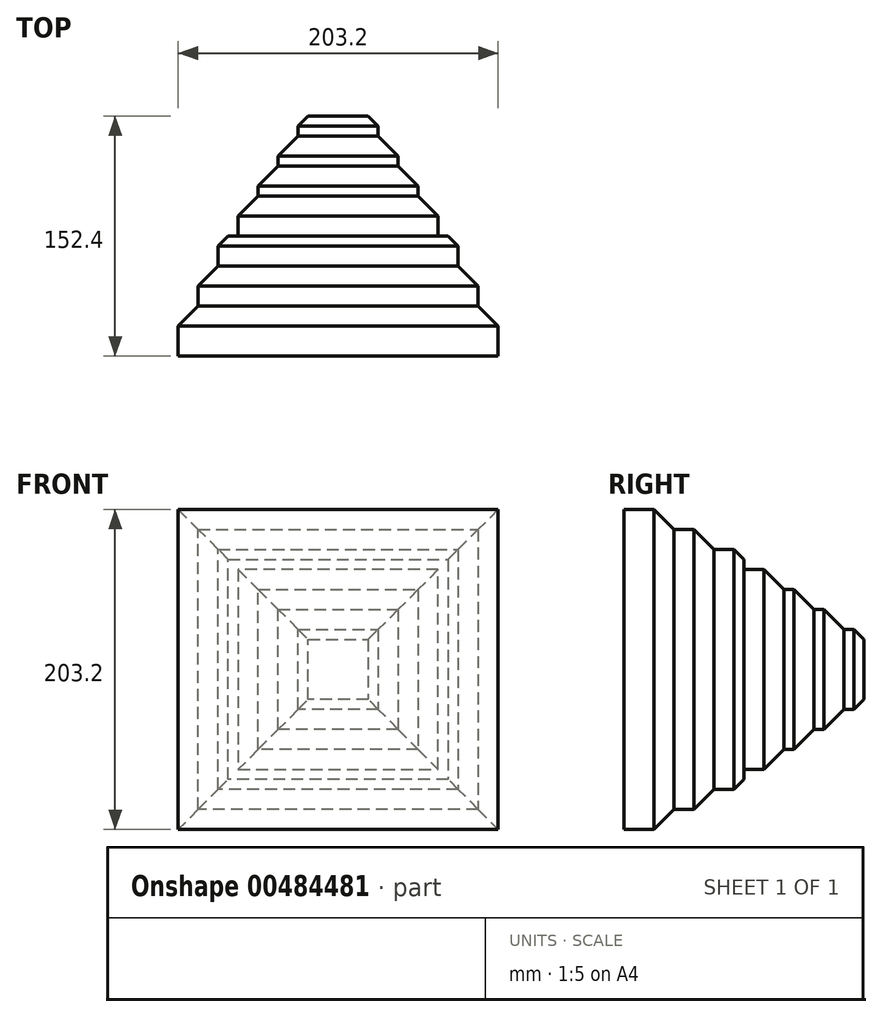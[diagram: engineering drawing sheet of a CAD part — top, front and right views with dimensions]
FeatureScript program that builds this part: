
annotation { "Feature Type Name" : "Feature", "Feature Type Description" : "" }
export const myFeature = defineFeature(function(context is Context, id is Id, definition is map)
    precondition{}
    {
        {
            var Q0;
            Q0=qCreatedBy(makeId("Front.planeOp"),FACE);
            var sketch = newSketch(context, id + "F0", { "sketchPlane" : qUnion([Q0])});
            skLineSegment(sketch, "E0.bottom", {"start": v(0, 0) * mm, "end": v(101.6, 0) * mm});
            skLineSegment(sketch, "E0.top", {"start": v(0, 101.6) * mm, "end": v(101.6, 101.6) * mm});
            skLineSegment(sketch, "E0.left", {"start": v(0, 0) * mm, "end": v(0, 101.6) * mm});
            skLineSegment(sketch, "E0.right", {"start": v(101.6, 0) * mm, "end": v(101.6, 101.6) * mm});
            skLineSegment(sketch, "E1.top", {"start": v(0, -101.6) * mm, "end": v(101.6, -101.6) * mm});
            skLineSegment(sketch, "E1.left", {"start": v(0, 0) * mm, "end": v(0, -101.6) * mm});
            skLineSegment(sketch, "E1.right", {"start": v(101.6, 0) * mm, "end": v(101.6, -101.6) * mm});
            skLineSegment(sketch, "E2.bottom", {"start": v(0, 0) * mm, "end": v(-101.6, 0) * mm});
            skLineSegment(sketch, "E2.top", {"start": v(0, -101.6) * mm, "end": v(-101.6, -101.6) * mm});
            skLineSegment(sketch, "E2.right", {"start": v(-101.6, 0) * mm, "end": v(-101.6, -101.6) * mm});
            skLineSegment(sketch, "E3.top", {"start": v(0, 101.6) * mm, "end": v(-101.6, 101.6) * mm});
            skLineSegment(sketch, "E3.right", {"start": v(-101.6, 0) * mm, "end": v(-101.6, 101.6) * mm});
            skSolve(sketch);
        }
        {
            var Q0;
            Q0=makeQuery(id+"F0.imprint","IMPRINT",FACE,{"disambiguationData":[TD([[makeQuery(id+"F0.imprint","IMPRINT",EDGE,{"derivedFrom":sQuery(id+"F0.wireOp",EDGE,"E2.bottom")}),-1.0]])]});
            var Q1;
            Q1=makeQuery(id+"F0.imprint","IMPRINT",FACE,{"disambiguationData":[TD([[makeQuery(id+"F0.imprint","IMPRINT",EDGE,{"derivedFrom":sQuery(id+"F0.wireOp",EDGE,"E0.top")}),-1.0]])]});
            var Q2;
            Q2=makeQuery(id+"F0.imprint","IMPRINT",FACE,{"disambiguationData":[TD([[makeQuery(id+"F0.imprint","IMPRINT",EDGE,{"derivedFrom":sQuery(id+"F0.wireOp",EDGE,"E0.bottom")}),-1.0]])]});
            var Q3;
            Q3=makeQuery(id+"F0.imprint","IMPRINT",FACE,{"disambiguationData":[TD([[makeQuery(id+"F0.imprint","IMPRINT",EDGE,{"derivedFrom":sQuery(id+"F0.wireOp",EDGE,"E2.top")}),-1.0]])]});
            extrude(context, id + "F1", {"entities" : qUnion([Q0, Q1, Q2, Q3]), "oppositeDirection" : true, "depth" : 25.4 * mm});
        }
        {
            var Q0;
            Q0=makeQuery(id+"F1.opExtrude","CAP_FACE",FACE,{"disambiguationData":[OSD([sQuery(id+"F0.wireOp",EDGE,"E0.top"),sQuery(id+"F0.wireOp",EDGE,"E0.right"),sQuery(id+"F0.wireOp",EDGE,"E1.top"),sQuery(id+"F0.wireOp",EDGE,"E1.right"),sQuery(id+"F0.wireOp",EDGE,"E2.top"),sQuery(id+"F0.wireOp",EDGE,"E2.right"),sQuery(id+"F0.wireOp",EDGE,"E3.top"),sQuery(id+"F0.wireOp",EDGE,"E3.right")])],"isStart":false});
            var sketch = newSketch(context, id + "F2", { "sketchPlane" : qUnion([Q0])});
            skLineSegment(sketch, "E4.bottom", {"start": v(0, 0) * mm, "end": v(88.9, 0) * mm});
            skLineSegment(sketch, "E4.top", {"start": v(0, 88.9) * mm, "end": v(88.9, 88.9) * mm});
            skLineSegment(sketch, "E4.left", {"start": v(0, 0) * mm, "end": v(0, 88.9) * mm});
            skLineSegment(sketch, "E4.right", {"start": v(88.9, 0) * mm, "end": v(88.9, 88.9) * mm});
            skLineSegment(sketch, "E5.top", {"start": v(0, -88.9) * mm, "end": v(88.9, -88.9) * mm});
            skLineSegment(sketch, "E5.left", {"start": v(0, 0) * mm, "end": v(0, -88.9) * mm});
            skLineSegment(sketch, "E5.right", {"start": v(88.9, 0) * mm, "end": v(88.9, -88.9) * mm});
            skLineSegment(sketch, "E6.bottom", {"start": v(0, 0) * mm, "end": v(-88.9, 0) * mm});
            skLineSegment(sketch, "E6.top", {"start": v(0, -88.9) * mm, "end": v(-88.9, -88.9) * mm});
            skLineSegment(sketch, "E6.right", {"start": v(-88.9, 0) * mm, "end": v(-88.9, -88.9) * mm});
            skLineSegment(sketch, "E7.top", {"start": v(0, 88.9) * mm, "end": v(-88.9, 88.9) * mm});
            skLineSegment(sketch, "E7.right", {"start": v(-88.9, 0) * mm, "end": v(-88.9, 88.9) * mm});
            skSolve(sketch);
        }
        {
            var Q0;
            Q0=makeQuery(id+"F2.imprint","IMPRINT",FACE,{"disambiguationData":[TD([[makeQuery(id+"F2.imprint","IMPRINT",EDGE,{"derivedFrom":sQuery(id+"F2.wireOp",EDGE,"E6.bottom")}),-1.0]])]});
            var Q1;
            Q1=makeQuery(id+"F2.imprint","IMPRINT",FACE,{"disambiguationData":[TD([[makeQuery(id+"F2.imprint","IMPRINT",EDGE,{"derivedFrom":sQuery(id+"F2.wireOp",EDGE,"E4.top")}),-1.0]])]});
            var Q2;
            Q2=makeQuery(id+"F2.imprint","IMPRINT",FACE,{"disambiguationData":[TD([[makeQuery(id+"F2.imprint","IMPRINT",EDGE,{"derivedFrom":sQuery(id+"F2.wireOp",EDGE,"E4.bottom")}),-1.0]])]});
            var Q3;
            Q3=makeQuery(id+"F2.imprint","IMPRINT",FACE,{"disambiguationData":[TD([[makeQuery(id+"F2.imprint","IMPRINT",EDGE,{"derivedFrom":sQuery(id+"F2.wireOp",EDGE,"E6.top")}),-1.0]])]});
            extrude(context, id + "F3", {"entities" : qUnion([Q0, Q1, Q2, Q3]), "operationType" : NewBodyOperationType.ADD, "depth" : 25.4 * mm});
        }
        {
            var Q0;
            Q0=makeQuery(id+"F3.opExtrude","CAP_FACE",FACE,{"disambiguationData":[OSD([sQuery(id+"F2.wireOp",EDGE,"E4.top"),sQuery(id+"F2.wireOp",EDGE,"E4.right"),sQuery(id+"F2.wireOp",EDGE,"E5.top"),sQuery(id+"F2.wireOp",EDGE,"E5.right"),sQuery(id+"F2.wireOp",EDGE,"E6.top"),sQuery(id+"F2.wireOp",EDGE,"E6.right"),sQuery(id+"F2.wireOp",EDGE,"E7.top"),sQuery(id+"F2.wireOp",EDGE,"E7.right")])],"isStart":false});
            var sketch = newSketch(context, id + "F4", { "sketchPlane" : qUnion([Q0])});
            skLineSegment(sketch, "E8.bottom", {"start": v(0, 0) * mm, "end": v(-76.2, 0) * mm});
            skLineSegment(sketch, "E8.top", {"start": v(0, -76.2) * mm, "end": v(-76.2, -76.2) * mm});
            skLineSegment(sketch, "E8.left", {"start": v(0, 0) * mm, "end": v(0, -76.2) * mm});
            skLineSegment(sketch, "E8.right", {"start": v(-76.2, 0) * mm, "end": v(-76.2, -76.2) * mm});
            skLineSegment(sketch, "E9.bottom", {"start": v(0, 0) * mm, "end": v(76.2, 0) * mm});
            skLineSegment(sketch, "E9.top", {"start": v(0, -76.2) * mm, "end": v(76.2, -76.2) * mm});
            skLineSegment(sketch, "E9.right", {"start": v(76.2, 0) * mm, "end": v(76.2, -76.2) * mm});
            skLineSegment(sketch, "E10.top", {"start": v(0, 76.2) * mm, "end": v(76.2, 76.2) * mm});
            skLineSegment(sketch, "E10.left", {"start": v(0, 0) * mm, "end": v(0, 76.2) * mm});
            skLineSegment(sketch, "E10.right", {"start": v(76.2, 0) * mm, "end": v(76.2, 76.2) * mm});
            skLineSegment(sketch, "E11.top", {"start": v(0, 76.2) * mm, "end": v(-76.2, 76.2) * mm});
            skLineSegment(sketch, "E11.right", {"start": v(-76.2, 0) * mm, "end": v(-76.2, 76.2) * mm});
            skSolve(sketch);
        }
        {
            var Q0;
            Q0=makeQuery(id+"F4.imprint","IMPRINT",FACE,{"disambiguationData":[TD([[makeQuery(id+"F4.imprint","IMPRINT",EDGE,{"derivedFrom":sQuery(id+"F4.wireOp",EDGE,"E8.bottom")}),-1.0]])]});
            var Q1;
            Q1=makeQuery(id+"F4.imprint","IMPRINT",FACE,{"disambiguationData":[TD([[makeQuery(id+"F4.imprint","IMPRINT",EDGE,{"derivedFrom":sQuery(id+"F4.wireOp",EDGE,"E9.bottom")}),1.0]])]});
            var Q2;
            Q2=makeQuery(id+"F4.imprint","IMPRINT",FACE,{"disambiguationData":[TD([[makeQuery(id+"F4.imprint","IMPRINT",EDGE,{"derivedFrom":sQuery(id+"F4.wireOp",EDGE,"E9.top")}),1.0]])]});
            var Q3;
            Q3=makeQuery(id+"F4.imprint","IMPRINT",FACE,{"disambiguationData":[TD([[makeQuery(id+"F4.imprint","IMPRINT",EDGE,{"derivedFrom":sQuery(id+"F4.wireOp",EDGE,"E8.top")}),-1.0]])]});
            var Q4;
            Q4 = qSketchRegion(id + "F6", true);
            extrude(context, id + "F5", {"entities" : qUnion([Q0, Q1, Q2, Q3, Q4]), "operationType" : NewBodyOperationType.ADD, "depth" : 25.4 * mm});
        }
        {
            var Q0;
            Q0=makeQuery(id+"F5.opExtrude","CAP_FACE",FACE,{"disambiguationData":[OSD([sQuery(id+"F4.wireOp",EDGE,"E8.top"),sQuery(id+"F4.wireOp",EDGE,"E8.right"),sQuery(id+"F4.wireOp",EDGE,"E9.top"),sQuery(id+"F4.wireOp",EDGE,"E9.right"),sQuery(id+"F4.wireOp",EDGE,"E10.top"),sQuery(id+"F4.wireOp",EDGE,"E10.right"),sQuery(id+"F4.wireOp",EDGE,"E11.top"),sQuery(id+"F4.wireOp",EDGE,"E11.right")])],"isStart":false});
            var sketch = newSketch(context, id + "F6", { "sketchPlane" : qUnion([Q0])});
            skLineSegment(sketch, "E12.bottom", {"start": v(0, 0) * mm, "end": v(-63.5, 0) * mm});
            skLineSegment(sketch, "E12.top", {"start": v(0, -63.5) * mm, "end": v(-63.5, -63.5) * mm});
            skLineSegment(sketch, "E12.left", {"start": v(0, 0) * mm, "end": v(0, -63.5) * mm});
            skLineSegment(sketch, "E12.right", {"start": v(-63.5, 0) * mm, "end": v(-63.5, -63.5) * mm});
            skLineSegment(sketch, "E13.bottom", {"start": v(0, 0) * mm, "end": v(63.5, 0) * mm});
            skLineSegment(sketch, "E13.top", {"start": v(0, -63.5) * mm, "end": v(63.5, -63.5) * mm});
            skLineSegment(sketch, "E13.right", {"start": v(63.5, 0) * mm, "end": v(63.5, -63.5) * mm});
            skLineSegment(sketch, "E14.top", {"start": v(0, 63.5) * mm, "end": v(63.5, 63.5) * mm});
            skLineSegment(sketch, "E14.left", {"start": v(0, 0) * mm, "end": v(0, 63.5) * mm});
            skLineSegment(sketch, "E14.right", {"start": v(63.5, 0) * mm, "end": v(63.5, 63.5) * mm});
            skLineSegment(sketch, "E15.top", {"start": v(0, 63.5) * mm, "end": v(-63.5, 63.5) * mm});
            skLineSegment(sketch, "E15.right", {"start": v(-63.5, 0) * mm, "end": v(-63.5, 63.5) * mm});
            skSolve(sketch);
        }
        {
            var Q0;
            Q0=makeQuery(id+"F6.imprint","IMPRINT",FACE,{"disambiguationData":[TD([[makeQuery(id+"F6.imprint","IMPRINT",EDGE,{"derivedFrom":sQuery(id+"F6.wireOp",EDGE,"E13.bottom")}),1.0]])]});
            var Q1;
            Q1=makeQuery(id+"F6.imprint","IMPRINT",FACE,{"disambiguationData":[TD([[makeQuery(id+"F6.imprint","IMPRINT",EDGE,{"derivedFrom":sQuery(id+"F6.wireOp",EDGE,"E12.bottom")}),-1.0]])]});
            var Q2;
            Q2=makeQuery(id+"F6.imprint","IMPRINT",FACE,{"disambiguationData":[TD([[makeQuery(id+"F6.imprint","IMPRINT",EDGE,{"derivedFrom":sQuery(id+"F6.wireOp",EDGE,"E12.top")}),-1.0]])]});
            var Q3;
            Q3=makeQuery(id+"F6.imprint","IMPRINT",FACE,{"disambiguationData":[TD([[makeQuery(id+"F6.imprint","IMPRINT",EDGE,{"derivedFrom":sQuery(id+"F6.wireOp",EDGE,"E13.top")}),1.0]])]});
            extrude(context, id + "F7", {"entities" : qUnion([Q0, Q1, Q2, Q3]), "depth" : 19.05 * mm});
        }
        {
            var Q0;
            Q0=makeQuery(id+"F7.opExtrude","CAP_FACE",FACE,{"disambiguationData":[OSD([sQuery(id+"F6.wireOp",EDGE,"E12.top"),sQuery(id+"F6.wireOp",EDGE,"E12.right"),sQuery(id+"F6.wireOp",EDGE,"E13.top"),sQuery(id+"F6.wireOp",EDGE,"E13.right"),sQuery(id+"F6.wireOp",EDGE,"E14.top"),sQuery(id+"F6.wireOp",EDGE,"E14.right"),sQuery(id+"F6.wireOp",EDGE,"E15.top"),sQuery(id+"F6.wireOp",EDGE,"E15.right")])],"isStart":false});
            var sketch = newSketch(context, id + "F8", { "sketchPlane" : qUnion([Q0])});
            skLineSegment(sketch, "E16.bottom", {"start": v(0, 0) * mm, "end": v(-50.8, 0) * mm});
            skLineSegment(sketch, "E16.top", {"start": v(0, -50.8) * mm, "end": v(-50.8, -50.8) * mm});
            skLineSegment(sketch, "E16.left", {"start": v(0, 0) * mm, "end": v(0, -50.8) * mm});
            skLineSegment(sketch, "E16.right", {"start": v(-50.8, 0) * mm, "end": v(-50.8, -50.8) * mm});
            skLineSegment(sketch, "E17.bottom", {"start": v(0, 0) * mm, "end": v(50.8, 0) * mm});
            skLineSegment(sketch, "E17.top", {"start": v(0, -50.8) * mm, "end": v(50.8, -50.8) * mm});
            skLineSegment(sketch, "E17.right", {"start": v(50.8, 0) * mm, "end": v(50.8, -50.8) * mm});
            skLineSegment(sketch, "E18.top", {"start": v(0, 50.8) * mm, "end": v(50.8, 50.8) * mm});
            skLineSegment(sketch, "E18.left", {"start": v(0, 0) * mm, "end": v(0, 50.8) * mm});
            skLineSegment(sketch, "E18.right", {"start": v(50.8, 0) * mm, "end": v(50.8, 50.8) * mm});
            skLineSegment(sketch, "E19.top", {"start": v(0, 50.8) * mm, "end": v(-50.8, 50.8) * mm});
            skLineSegment(sketch, "E19.right", {"start": v(-50.8, 0) * mm, "end": v(-50.8, 50.8) * mm});
            skSolve(sketch);
        }
        {
            var Q0;
            Q0=makeQuery(id+"F8.imprint","IMPRINT",FACE,{"disambiguationData":[TD([[makeQuery(id+"F8.imprint","IMPRINT",EDGE,{"derivedFrom":sQuery(id+"F8.wireOp",EDGE,"E16.top")}),-1.0]])]});
            var Q1;
            Q1=makeQuery(id+"F8.imprint","IMPRINT",FACE,{"disambiguationData":[TD([[makeQuery(id+"F8.imprint","IMPRINT",EDGE,{"derivedFrom":sQuery(id+"F8.wireOp",EDGE,"E17.top")}),1.0]])]});
            var Q2;
            Q2=makeQuery(id+"F8.imprint","IMPRINT",FACE,{"disambiguationData":[TD([[makeQuery(id+"F8.imprint","IMPRINT",EDGE,{"derivedFrom":sQuery(id+"F8.wireOp",EDGE,"E16.bottom")}),-1.0]])]});
            var Q3;
            Q3=makeQuery(id+"F8.imprint","IMPRINT",FACE,{"disambiguationData":[TD([[makeQuery(id+"F8.imprint","IMPRINT",EDGE,{"derivedFrom":sQuery(id+"F8.wireOp",EDGE,"E17.bottom")}),1.0]])]});
            extrude(context, id + "F9", {"entities" : qUnion([Q0, Q1, Q2, Q3]), "operationType" : NewBodyOperationType.ADD, "depth" : 19.05 * mm});
        }
        {
            var Q0;
            Q0=makeQuery(id+"F9.opExtrude","CAP_FACE",FACE,{"disambiguationData":[OSD([sQuery(id+"F8.wireOp",EDGE,"E16.top"),sQuery(id+"F8.wireOp",EDGE,"E16.right"),sQuery(id+"F8.wireOp",EDGE,"E17.top"),sQuery(id+"F8.wireOp",EDGE,"E17.right"),sQuery(id+"F8.wireOp",EDGE,"E18.top"),sQuery(id+"F8.wireOp",EDGE,"E18.right"),sQuery(id+"F8.wireOp",EDGE,"E19.top"),sQuery(id+"F8.wireOp",EDGE,"E19.right")])],"isStart":false});
            var sketch = newSketch(context, id + "F10", { "sketchPlane" : qUnion([Q0])});
            skLineSegment(sketch, "E20.bottom", {"start": v(0, 0) * mm, "end": v(-38.1, 0) * mm});
            skLineSegment(sketch, "E20.top", {"start": v(0, 38.1) * mm, "end": v(-38.1, 38.1) * mm});
            skLineSegment(sketch, "E20.left", {"start": v(0, 0) * mm, "end": v(0, 38.1) * mm});
            skLineSegment(sketch, "E20.right", {"start": v(-38.1, 0) * mm, "end": v(-38.1, 38.1) * mm});
            skLineSegment(sketch, "E21.bottom", {"start": v(0, 0) * mm, "end": v(38.1, 0) * mm});
            skLineSegment(sketch, "E21.top", {"start": v(0, 38.1) * mm, "end": v(38.1, 38.1) * mm});
            skLineSegment(sketch, "E21.right", {"start": v(38.1, 0) * mm, "end": v(38.1, 38.1) * mm});
            skLineSegment(sketch, "E22.top", {"start": v(0, -38.1) * mm, "end": v(38.1, -38.1) * mm});
            skLineSegment(sketch, "E22.left", {"start": v(0, 0) * mm, "end": v(0, -38.1) * mm});
            skLineSegment(sketch, "E22.right", {"start": v(38.1, 0) * mm, "end": v(38.1, -38.1) * mm});
            skLineSegment(sketch, "E23.top", {"start": v(0, -38.1) * mm, "end": v(-38.1, -38.1) * mm});
            skLineSegment(sketch, "E23.right", {"start": v(-38.1, 0) * mm, "end": v(-38.1, -38.1) * mm});
            skSolve(sketch);
        }
        {
            var Q0;
            Q0=makeQuery(id+"F10.imprint","IMPRINT",FACE,{"disambiguationData":[TD([[makeQuery(id+"F10.imprint","IMPRINT",EDGE,{"derivedFrom":sQuery(id+"F10.wireOp",EDGE,"E21.top")}),-1.0]])]});
            var Q1;
            Q1=makeQuery(id+"F10.imprint","IMPRINT",FACE,{"disambiguationData":[TD([[makeQuery(id+"F10.imprint","IMPRINT",EDGE,{"derivedFrom":sQuery(id+"F10.wireOp",EDGE,"E21.bottom")}),-1.0]])]});
            var Q2;
            Q2=makeQuery(id+"F10.imprint","IMPRINT",FACE,{"disambiguationData":[TD([[makeQuery(id+"F10.imprint","IMPRINT",EDGE,{"derivedFrom":sQuery(id+"F10.wireOp",EDGE,"E20.bottom")}),1.0]])]});
            var Q3;
            Q3=makeQuery(id+"F10.imprint","IMPRINT",FACE,{"disambiguationData":[TD([[makeQuery(id+"F10.imprint","IMPRINT",EDGE,{"derivedFrom":sQuery(id+"F10.wireOp",EDGE,"E20.top")}),1.0]])]});
            extrude(context, id + "F11", {"entities" : qUnion([Q0, Q1, Q2, Q3]), "operationType" : NewBodyOperationType.ADD, "depth" : 19.05 * mm});
        }
        {
            var Q0;
            Q0=makeQuery(id+"F11.opExtrude","CAP_FACE",FACE,{"disambiguationData":[OSD([sQuery(id+"F10.wireOp",EDGE,"E20.top"),sQuery(id+"F10.wireOp",EDGE,"E20.right"),sQuery(id+"F10.wireOp",EDGE,"E21.top"),sQuery(id+"F10.wireOp",EDGE,"E21.right"),sQuery(id+"F10.wireOp",EDGE,"E22.top"),sQuery(id+"F10.wireOp",EDGE,"E22.right"),sQuery(id+"F10.wireOp",EDGE,"E23.top"),sQuery(id+"F10.wireOp",EDGE,"E23.right")])],"isStart":false});
            var sketch = newSketch(context, id + "F12", { "sketchPlane" : qUnion([Q0])});
            skLineSegment(sketch, "E24.bottom", {"start": v(0, 0) * mm, "end": v(-25.4, 0) * mm});
            skLineSegment(sketch, "E24.top", {"start": v(0, 25.4) * mm, "end": v(-25.4, 25.4) * mm});
            skLineSegment(sketch, "E24.left", {"start": v(0, 0) * mm, "end": v(0, 25.4) * mm});
            skLineSegment(sketch, "E24.right", {"start": v(-25.4, 0) * mm, "end": v(-25.4, 25.4) * mm});
            skLineSegment(sketch, "E25.bottom", {"start": v(0, 0) * mm, "end": v(25.4, 0) * mm});
            skLineSegment(sketch, "E25.top", {"start": v(0, 25.4) * mm, "end": v(25.4, 25.4) * mm});
            skLineSegment(sketch, "E25.right", {"start": v(25.4, 0) * mm, "end": v(25.4, 25.4) * mm});
            skLineSegment(sketch, "E26.top", {"start": v(0, -25.4) * mm, "end": v(25.4, -25.4) * mm});
            skLineSegment(sketch, "E26.left", {"start": v(0, 0) * mm, "end": v(0, -25.4) * mm});
            skLineSegment(sketch, "E26.right", {"start": v(25.4, 0) * mm, "end": v(25.4, -25.4) * mm});
            skLineSegment(sketch, "E27.top", {"start": v(0, -25.4) * mm, "end": v(-25.4, -25.4) * mm});
            skLineSegment(sketch, "E27.right", {"start": v(-25.4, 0) * mm, "end": v(-25.4, -25.4) * mm});
            skSolve(sketch);
        }
        {
            var Q0;
            Q0 = qSketchRegion(id + "F12", true);
            extrude(context, id + "F13", {"entities" : qUnion([Q0]), "operationType" : NewBodyOperationType.ADD, "depth" : 19.05 * mm});
        }
        {
            var Q0;
            Q0=makeQuery(id+"F13.opExtrude","CAP_FACE",FACE,{"disambiguationData":[OSD([sQuery(id+"F12.wireOp",EDGE,"E24.top"),sQuery(id+"F12.wireOp",EDGE,"E24.right"),sQuery(id+"F12.wireOp",EDGE,"E25.top"),sQuery(id+"F12.wireOp",EDGE,"E25.right"),sQuery(id+"F12.wireOp",EDGE,"E26.top"),sQuery(id+"F12.wireOp",EDGE,"E26.right"),sQuery(id+"F12.wireOp",EDGE,"E27.top"),sQuery(id+"F12.wireOp",EDGE,"E27.right")])],"isStart":false});
            var Q1;
            Q1=makeQuery(id+"F11.opExtrude","CAP_FACE",FACE,{"disambiguationData":[OSD([sQuery(id+"F10.wireOp",EDGE,"E20.top"),sQuery(id+"F10.wireOp",EDGE,"E20.right"),sQuery(id+"F10.wireOp",EDGE,"E21.top"),sQuery(id+"F10.wireOp",EDGE,"E21.right"),sQuery(id+"F10.wireOp",EDGE,"E22.top"),sQuery(id+"F10.wireOp",EDGE,"E22.right"),sQuery(id+"F10.wireOp",EDGE,"E23.top"),sQuery(id+"F10.wireOp",EDGE,"E23.right")])],"isStart":false});
            var Q2;
            Q2=makeQuery(id+"F9.opExtrude","CAP_FACE",FACE,{"disambiguationData":[OSD([sQuery(id+"F8.wireOp",EDGE,"E16.top"),sQuery(id+"F8.wireOp",EDGE,"E16.right"),sQuery(id+"F8.wireOp",EDGE,"E17.top"),sQuery(id+"F8.wireOp",EDGE,"E17.right"),sQuery(id+"F8.wireOp",EDGE,"E18.top"),sQuery(id+"F8.wireOp",EDGE,"E18.right"),sQuery(id+"F8.wireOp",EDGE,"E19.top"),sQuery(id+"F8.wireOp",EDGE,"E19.right")])],"isStart":false});
            var Q3;
            Q3=makeQuery(id+"F7.opExtrude","CAP_FACE",FACE,{"disambiguationData":[OSD([sQuery(id+"F6.wireOp",EDGE,"E12.top"),sQuery(id+"F6.wireOp",EDGE,"E12.right"),sQuery(id+"F6.wireOp",EDGE,"E13.top"),sQuery(id+"F6.wireOp",EDGE,"E13.right"),sQuery(id+"F6.wireOp",EDGE,"E14.top"),sQuery(id+"F6.wireOp",EDGE,"E14.right"),sQuery(id+"F6.wireOp",EDGE,"E15.top"),sQuery(id+"F6.wireOp",EDGE,"E15.right")])],"isStart":false});
            var Q4;
            Q4=makeQuery(id+"F5.opExtrude","CAP_FACE",FACE,{"disambiguationData":[OSD([sQuery(id+"F4.wireOp",EDGE,"E8.top"),sQuery(id+"F4.wireOp",EDGE,"E8.right"),sQuery(id+"F4.wireOp",EDGE,"E9.top"),sQuery(id+"F4.wireOp",EDGE,"E9.right"),sQuery(id+"F4.wireOp",EDGE,"E10.top"),sQuery(id+"F4.wireOp",EDGE,"E10.right"),sQuery(id+"F4.wireOp",EDGE,"E11.top"),sQuery(id+"F4.wireOp",EDGE,"E11.right")])],"isStart":false});
            var Q5;
            Q5=makeQuery(id+"F3.opExtrude","CAP_FACE",FACE,{"disambiguationData":[OSD([sQuery(id+"F2.wireOp",EDGE,"E4.top"),sQuery(id+"F2.wireOp",EDGE,"E4.right"),sQuery(id+"F2.wireOp",EDGE,"E5.top"),sQuery(id+"F2.wireOp",EDGE,"E5.right"),sQuery(id+"F2.wireOp",EDGE,"E6.top"),sQuery(id+"F2.wireOp",EDGE,"E6.right"),sQuery(id+"F2.wireOp",EDGE,"E7.top"),sQuery(id+"F2.wireOp",EDGE,"E7.right")])],"isStart":false});
            var Q6;
            Q6=makeQuery(id+"F1.opExtrude","CAP_FACE",FACE,{"disambiguationData":[OSD([sQuery(id+"F0.wireOp",EDGE,"E0.top"),sQuery(id+"F0.wireOp",EDGE,"E0.right"),sQuery(id+"F0.wireOp",EDGE,"E1.top"),sQuery(id+"F0.wireOp",EDGE,"E1.right"),sQuery(id+"F0.wireOp",EDGE,"E2.top"),sQuery(id+"F0.wireOp",EDGE,"E2.right"),sQuery(id+"F0.wireOp",EDGE,"E3.top"),sQuery(id+"F0.wireOp",EDGE,"E3.right")])],"isStart":false});
            chamfer(context, id + "F14", {"entities" : qUnion([Q0, Q1, Q2, Q3, Q4, Q5, Q6]), "width" : 6.35 * mm, "tangentPropagation" : true});
        }
    });
